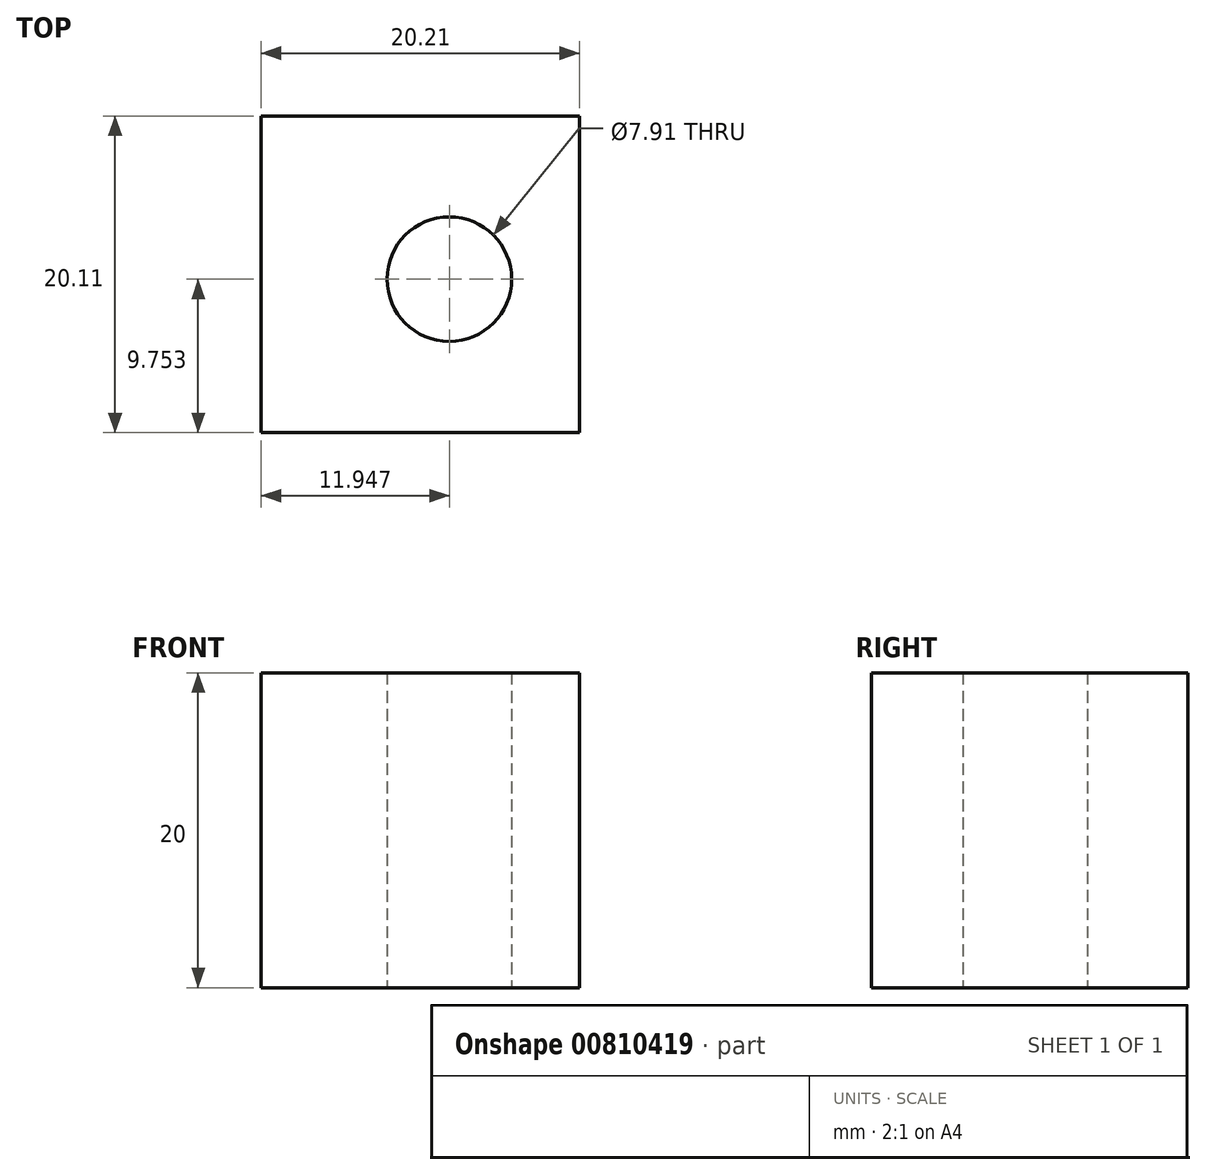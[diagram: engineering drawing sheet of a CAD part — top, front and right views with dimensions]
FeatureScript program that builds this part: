
annotation { "Feature Type Name" : "Feature", "Feature Type Description" : "" }
export const myFeature = defineFeature(function(context is Context, id is Id, definition is map)
    precondition{}
    {
        {
            var Q0;
            Q0=qCreatedBy(makeId("Top.planeOp"),FACE);
            var sketch = newSketch(context, id + "F0", { "sketchPlane" : qUnion([Q0])});
            skLineSegment(sketch, "E0.bottom", {"start": v(0, 0) * mm, "end": v(-20.2, 0) * mm});
            skLineSegment(sketch, "E0.top", {"start": v(0, -20.11) * mm, "end": v(-20.2, -20.11) * mm});
            skLineSegment(sketch, "E0.left", {"start": v(0, 0) * mm, "end": v(0, -20.11) * mm});
            skLineSegment(sketch, "E0.right", {"start": v(-20.2, 0) * mm, "end": v(-20.2, -20.11) * mm});
            skSolve(sketch);
        }
        {
            var Q0;
            Q0 = qSketchRegion(id + "F0", true);
            extrude(context, id + "F1", {"entities" : qUnion([Q0]), "depth" : 20 * mm, "offsetDistance" : 25 * mm});
        }
        {
            var Q0;
            Q0=makeQuery(id+"F1.opExtrude","CAP_FACE",FACE,{"disambiguationData":[OSD([sQuery(id+"F0.wireOp",EDGE,"E0.bottom"),sQuery(id+"F0.wireOp",EDGE,"E0.top"),sQuery(id+"F0.wireOp",EDGE,"E0.left"),sQuery(id+"F0.wireOp",EDGE,"E0.right")])],"isStart":true});
            var sketch = newSketch(context, id + "F2", { "sketchPlane" : qUnion([Q0])});
            skSolve(sketch);
        }
        {
            var Q0;
            Q0=makeQuery(id+"F2.imprint","IMPRINT",FACE,{"disambiguationData":[TD([[makeQuery(id+"F2.imprint","IMPRINT",EDGE,{"derivedFrom":makeQuery(id+"F1.opExtrude","CAP_EDGE",EDGE,{"disambiguationData":[OSD([sQuery(id+"F0.wireOp",EDGE,"E0.bottom")])],"isStart":true})}),-1.0]])]});
            var sketch = newSketch(context, id + "F3", { "sketchPlane" : qUnion([Q0])});
            skCircle(sketch, "E1", {"center": v(-8.26, 10.36) * mm, "radius": 3.96 * mm});
            skCircle(sketch, "E2", {"center": v(-8.26, 10.36) * mm, "radius": 2.3 * mm});
            skCircle(sketch, "E3", {"center": v(-8.26, 10.36) * mm, "radius": 1.33 * mm});
            skSolve(sketch);
        }
        {
            var Q0;
            Q0=makeQuery(id+"F3.imprint","IMPRINT",FACE,{"disambiguationData":[TD([[makeQuery(id+"F3.imprint","IMPRINT",EDGE,{"derivedFrom":sQuery(id+"F3.wireOp",EDGE,"E3")}),1.0]])]});
            var Q1;
            Q1=makeQuery(id+"F3.imprint","IMPRINT",FACE,{"disambiguationData":[TD([[makeQuery(id+"F3.imprint","IMPRINT",EDGE,{"derivedFrom":sQuery(id+"F3.wireOp",EDGE,"E2")}),1.0]])]});
            var Q2;
            Q2=makeQuery(id+"F3.imprint","IMPRINT",FACE,{"disambiguationData":[TD([[makeQuery(id+"F3.imprint","IMPRINT",EDGE,{"derivedFrom":sQuery(id+"F3.wireOp",EDGE,"E1")}),1.0]])]});
            extrude(context, id + "F4", {"entities" : qUnion([Q0, Q1, Q2]), "operationType" : NewBodyOperationType.REMOVE, "oppositeDirection" : true, "depth" : 25 * mm, "offsetDistance" : 25 * mm});
        }
    });
